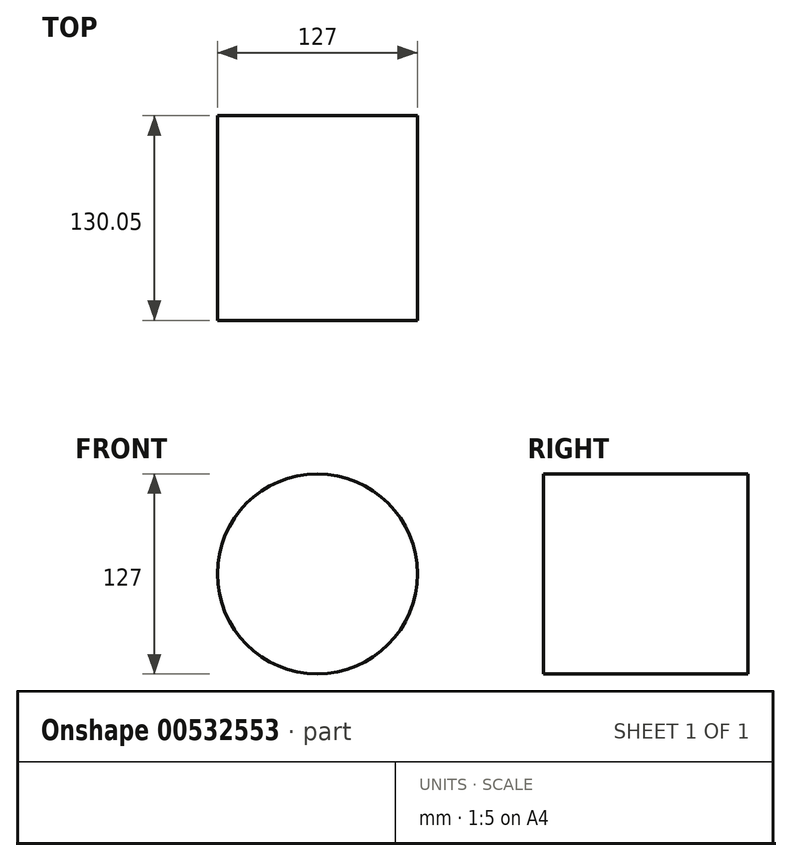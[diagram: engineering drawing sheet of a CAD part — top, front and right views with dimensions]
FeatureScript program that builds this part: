
annotation { "Feature Type Name" : "Feature", "Feature Type Description" : "" }
export const myFeature = defineFeature(function(context is Context, id is Id, definition is map)
    precondition{}
    {
        {
            var Q0;
            Q0=qCreatedBy(makeId("Front.planeOp"),FACE);
            var sketch = newSketch(context, id + "F0", { "sketchPlane" : qUnion([Q0])});
            skCircle(sketch, "E0", {"center": v(0, 0) * mm, "radius": 63.5 * mm});
            skSolve(sketch);
        }
        {
            var Q0;
            Q0=makeQuery(id+"F0.imprint","IMPRINT",FACE,{"disambiguationData":[TD([[makeQuery(id+"F0.imprint","IMPRINT",EDGE,{"derivedFrom":sQuery(id+"F0.wireOp",EDGE,"E0")}),1.0]])]});
            extrude(context, id + "F1", {"entities" : qUnion([Q0]), "depth" : 130.05 * mm, "offsetDistance" : 25.4 * mm});
        }
    });
